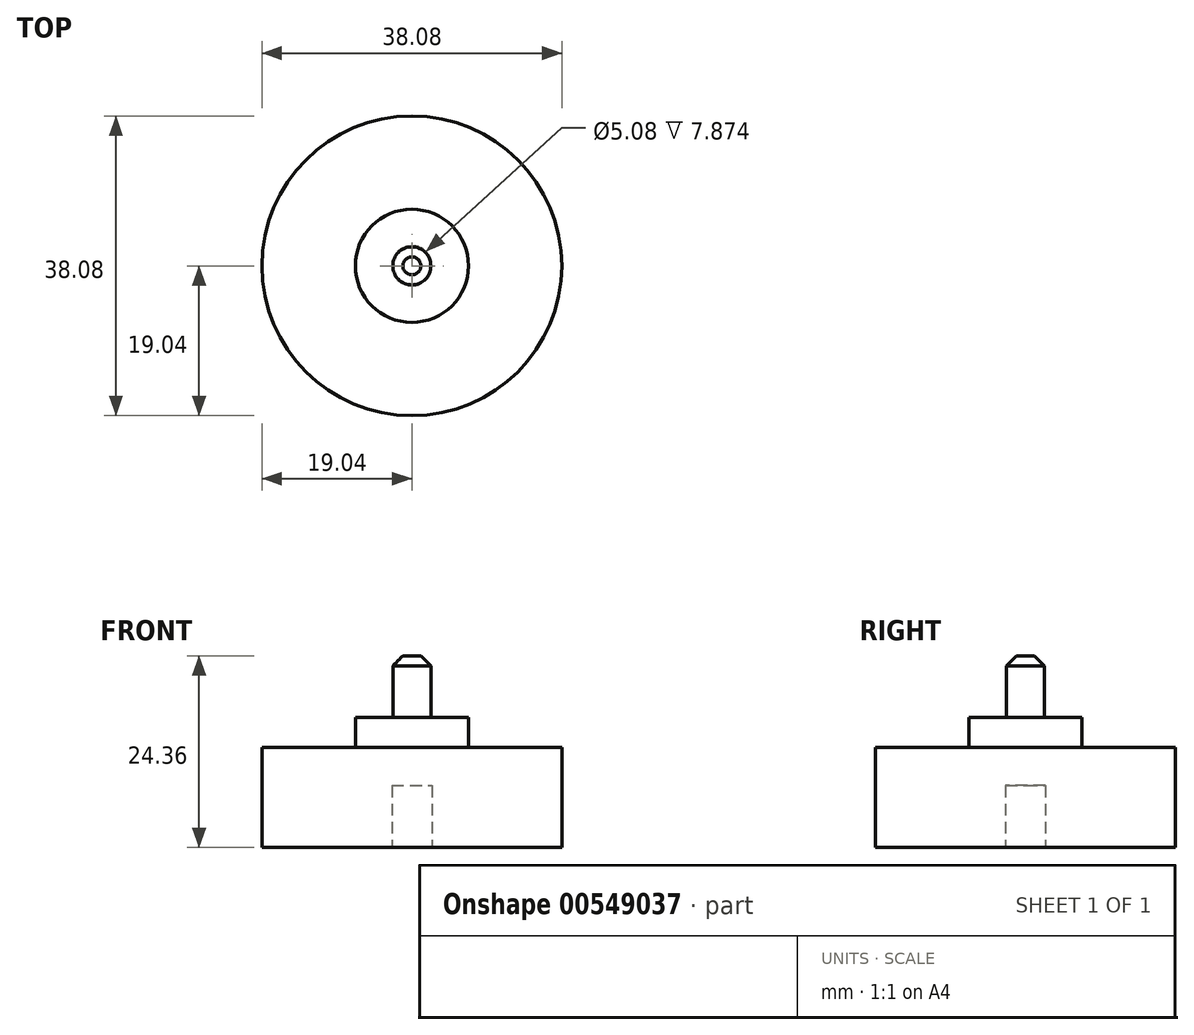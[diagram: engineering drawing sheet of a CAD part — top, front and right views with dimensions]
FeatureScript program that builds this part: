
annotation { "Feature Type Name" : "Feature", "Feature Type Description" : "" }
export const myFeature = defineFeature(function(context is Context, id is Id, definition is map)
    precondition{}
    {
        {
            var Q0;
            Q0=qCreatedBy(makeId("Front.planeOp"),FACE);
            var sketch = newSketch(context, id + "F0", { "sketchPlane" : qUnion([Q0])});
            skLineSegment(sketch, "E0", {"start": v(19.04, 0) * mm, "end": v(19.04, 12.7) * mm});
            skLineSegment(sketch, "E1", {"start": v(19.04, 12.7) * mm, "end": v(7.19, 12.7) * mm});
            skLineSegment(sketch, "E2", {"start": v(2.41, 16.51) * mm, "end": v(7.19, 16.51) * mm});
            skLineSegment(sketch, "E3", {"start": v(7.19, 16.51) * mm, "end": v(7.19, 12.7) * mm});
            skLineSegment(sketch, "E4", {"start": v(0, 24.36) * mm, "end": v(2.41, 24.36) * mm});
            skLineSegment(sketch, "E5", {"start": v(2.41, 24.36) * mm, "end": v(2.41, 16.51) * mm});
            skPoint(sketch, "E6.orphan", {"position": v(2.41, 12.7) * mm});
            skLineSegment(sketch, "E7", {"start": v(2.54, 0) * mm, "end": v(2.54, 7.87) * mm});
            skLineSegment(sketch, "E8", {"start": v(2.54, 7.87) * mm, "end": v(0, 7.87) * mm});
            skLineSegment(sketch, "E9", {"start": v(0, 7.87) * mm, "end": v(0, 24.36) * mm});
            skLineSegment(sketch, "E10", {"start": v(19.04, 0) * mm, "end": v(2.54, 0) * mm});
            skSolve(sketch);
        }
        {
            var Q0;
            Q0 = qSketchRegion(id + "F0", true);
            var Q1;
            Q1=sQuery(id+"F0.wireOp",EDGE,"E9");
            revolve(context, id + "F1", {"entities" : qUnion([Q0]), "axis" : qUnion([Q1]), "revolveType" : RevolveType.FULL});
        }
        {
            var Q0;
            Q0=makeQuery(id+"F1.opRevolve","SWEPT_EDGE",EDGE,{"disambiguationData":[OSD([sQuery(id+"F0.wireOp",EDGE,"E4"),sQuery(id+"F0.wireOp",EDGE,"E5")])]});
            chamfer(context, id + "F2", {"entities" : qUnion([Q0]), "width" : 1.27 * mm, "tangentPropagation" : true});
        }
    });
